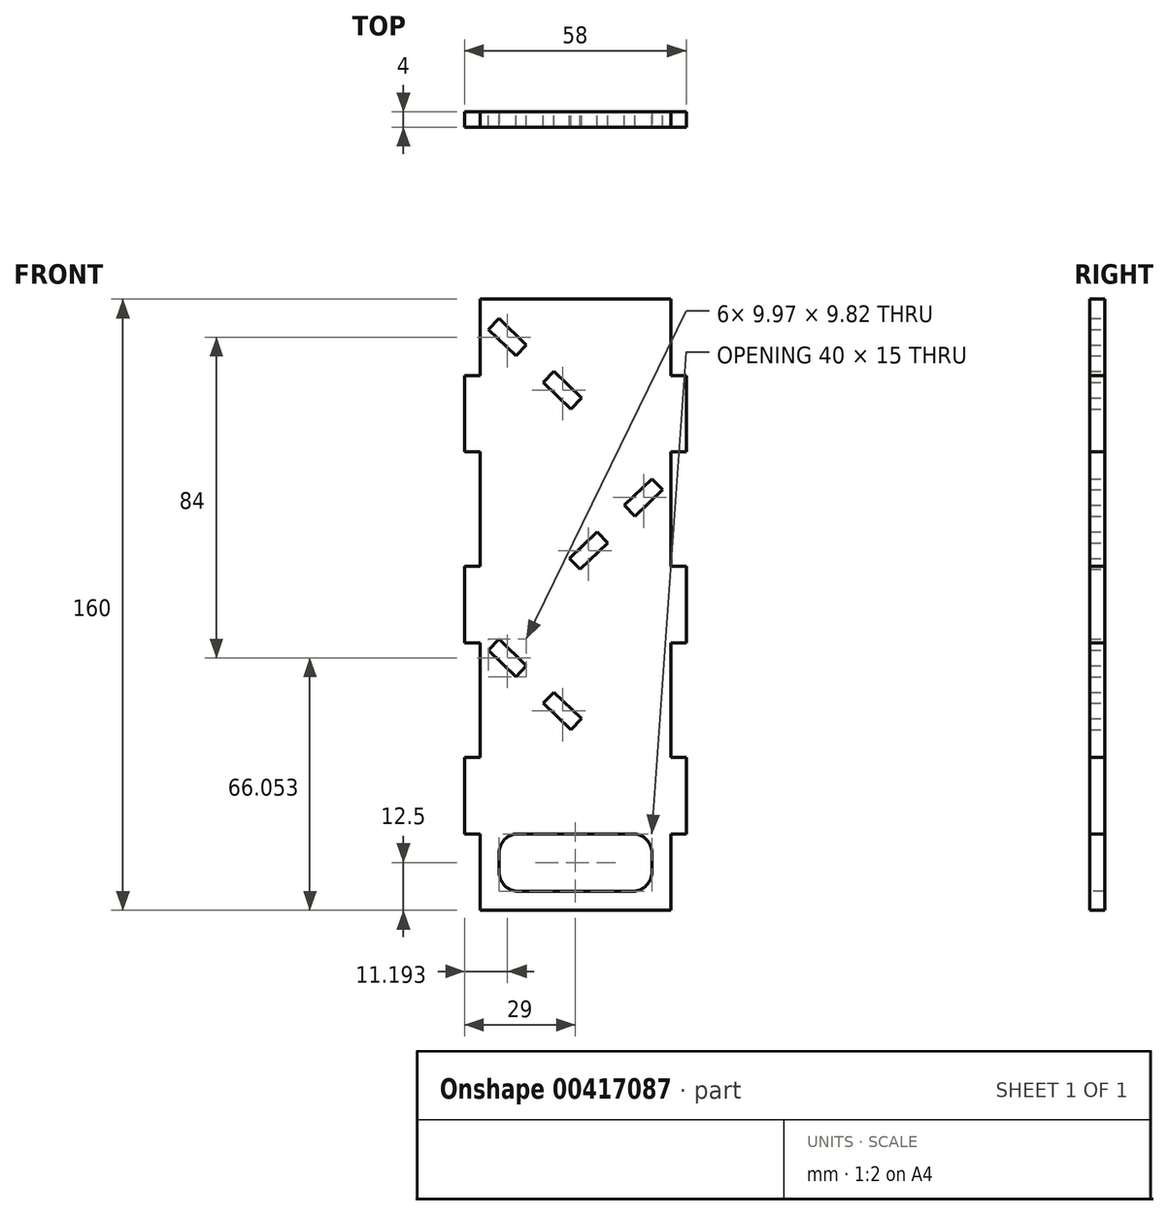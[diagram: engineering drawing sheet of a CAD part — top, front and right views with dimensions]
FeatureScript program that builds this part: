
annotation { "Feature Type Name" : "Feature", "Feature Type Description" : "" }
export const myFeature = defineFeature(function(context is Context, id is Id, definition is map)
    precondition{}
    {
        {
            var Q0;
            Q0=qCreatedBy(makeId("Front.planeOp"),FACE);
            var sketch = newSketch(context, id + "F0", { "sketchPlane" : qUnion([Q0])});
            skLineSegment(sketch, "E0.bottom", {"start": v(25, -80) * mm, "end": v(-25, -80) * mm});
            skLineSegment(sketch, "E0.top", {"start": v(25, 80) * mm, "end": v(-25, 80) * mm});
            skLineSegment(sketch, "E0.left", {"start": v(25, -80) * mm, "end": v(25, 80) * mm});
            skLineSegment(sketch, "E0.right", {"start": v(-25, -80) * mm, "end": v(-25, 80) * mm});
            skPoint(sketch, "E0.middle", {"position": v(0, 0) * mm});
            skLineSegment(sketch, "E1", {"start": v(-25, 77) * mm, "end": v(3.77, 49.21) * mm, "construction": true});
            skLineSegment(sketch, "E2", {"start": v(25, 34.96) * mm, "end": v(-3.77, 7.17) * mm, "construction": true});
            skLineSegment(sketch, "E3", {"start": v(-25, -7.08) * mm, "end": v(3.77, -34.87) * mm, "construction": true});
            skLineSegment(sketch, "E4", {"start": v(-21.4, 73.53) * mm, "end": v(-20.01, 74.97) * mm});
            skLineSegment(sketch, "E5", {"start": v(-20.01, 74.97) * mm, "end": v(-12.82, 68.02) * mm});
            skLineSegment(sketch, "E6", {"start": v(-12.82, 68.02) * mm, "end": v(-14.2, 66.58) * mm});
            skLineSegment(sketch, "E7", {"start": v(-7.02, 59.63) * mm, "end": v(-5.63, 61.07) * mm});
            skLineSegment(sketch, "E8", {"start": v(-5.63, 61.07) * mm, "end": v(1.57, 54.13) * mm});
            skLineSegment(sketch, "E9", {"start": v(1.57, 54.13) * mm, "end": v(0.18, 52.69) * mm});
            skLineSegment(sketch, "E10.MirrorCS", {"start": v(-21.4, 73.53) * mm, "end": v(-22.8, 72.09) * mm});
            skLineSegment(sketch, "E11.MirrorCS", {"start": v(-22.8, 72.09) * mm, "end": v(-15.6, 65.14) * mm});
            skLineSegment(sketch, "E12.MirrorCS", {"start": v(-15.6, 65.14) * mm, "end": v(-14.2, 66.58) * mm});
            skLineSegment(sketch, "E13.MirrorCS", {"start": v(-7.02, 59.63) * mm, "end": v(-8.4, 58.2) * mm});
            skLineSegment(sketch, "E14.MirrorCS", {"start": v(-8.4, 58.2) * mm, "end": v(-1.21, 51.25) * mm});
            skLineSegment(sketch, "E15.MirrorCS", {"start": v(-1.21, 51.25) * mm, "end": v(0.18, 52.69) * mm});
            skLineSegment(sketch, "E16.0.1.0", {"start": v(-8.4, 16.2) * mm, "end": v(-1.21, 9.25) * mm, "construction": true});
            skLineSegment(sketch, "E16.0.1.1", {"start": v(-20.01, 32.97) * mm, "end": v(-12.82, 26.02) * mm, "construction": true});
            skLineSegment(sketch, "E16.0.1.2", {"start": v(-5.63, 19.07) * mm, "end": v(1.57, 12.13) * mm, "construction": true});
            skLineSegment(sketch, "E16.0.1.3", {"start": v(-22.8, 30.09) * mm, "end": v(-15.6, 23.14) * mm, "construction": true});
            skLineSegment(sketch, "E16.0.1.4", {"start": v(-12.82, 26.02) * mm, "end": v(-14.2, 24.58) * mm, "construction": true});
            skLineSegment(sketch, "E16.0.1.5", {"start": v(-7.02, 17.63) * mm, "end": v(-5.63, 19.07) * mm, "construction": true});
            skLineSegment(sketch, "E16.0.1.6", {"start": v(-21.4, 31.53) * mm, "end": v(-20.01, 32.97) * mm, "construction": true});
            skLineSegment(sketch, "E16.0.1.7", {"start": v(-21.4, 31.53) * mm, "end": v(-22.8, 30.09) * mm, "construction": true});
            skLineSegment(sketch, "E16.0.1.8", {"start": v(1.57, 12.13) * mm, "end": v(0.18, 10.69) * mm, "construction": true});
            skLineSegment(sketch, "E16.0.1.9", {"start": v(-15.6, 23.14) * mm, "end": v(-14.2, 24.58) * mm, "construction": true});
            skLineSegment(sketch, "E16.0.1.10", {"start": v(-1.21, 9.25) * mm, "end": v(0.18, 10.69) * mm, "construction": true});
            skLineSegment(sketch, "E16.0.1.11", {"start": v(-7.02, 17.63) * mm, "end": v(-8.4, 16.2) * mm, "construction": true});
            skLineSegment(sketch, "E16.direction1", {"start": v(-22.8, 72.09) * mm, "end": v(2.55, 72.09) * mm, "construction": true});
            skLineSegment(sketch, "E16.direction2", {"start": v(-22.8, 72.09) * mm, "end": v(-22.8, 30.09) * mm, "construction": true});
            skLineSegment(sketch, "E17.0.0.2", {"start": v(-8.4, -25.8) * mm, "end": v(-1.21, -32.75) * mm});
            skLineSegment(sketch, "E17.3.0.2", {"start": v(-20.01, -9.03) * mm, "end": v(-12.82, -15.98) * mm});
            skLineSegment(sketch, "E17.6.0.2", {"start": v(-5.63, -22.93) * mm, "end": v(1.57, -29.87) * mm});
            skLineSegment(sketch, "E17.9.0.2", {"start": v(-22.8, -11.91) * mm, "end": v(-15.6, -18.86) * mm});
            skLineSegment(sketch, "E17.12.0.2", {"start": v(-12.82, -15.98) * mm, "end": v(-14.2, -17.42) * mm});
            skLineSegment(sketch, "E17.15.0.2", {"start": v(-7.02, -24.37) * mm, "end": v(-5.63, -22.93) * mm});
            skLineSegment(sketch, "E17.18.0.2", {"start": v(-21.4, -10.47) * mm, "end": v(-20.01, -9.03) * mm});
            skLineSegment(sketch, "E17.21.0.2", {"start": v(-21.4, -10.47) * mm, "end": v(-22.8, -11.91) * mm});
            skLineSegment(sketch, "E17.24.0.2", {"start": v(1.57, -29.87) * mm, "end": v(0.18, -31.31) * mm});
            skLineSegment(sketch, "E17.27.0.2", {"start": v(-15.6, -18.86) * mm, "end": v(-14.2, -17.42) * mm});
            skLineSegment(sketch, "E17.30.0.2", {"start": v(-1.21, -32.75) * mm, "end": v(0.18, -31.31) * mm});
            skLineSegment(sketch, "E17.33.0.2", {"start": v(-7.02, -24.37) * mm, "end": v(-8.4, -25.8) * mm});
            skLineSegment(sketch, "E18.MirrorCS", {"start": v(21.4, 31.53) * mm, "end": v(22.8, 30.09) * mm});
            skLineSegment(sketch, "E19.MirrorCS", {"start": v(21.4, 31.53) * mm, "end": v(20.01, 32.97) * mm});
            skLineSegment(sketch, "E20.MirrorCS", {"start": v(7.02, 17.63) * mm, "end": v(8.4, 16.2) * mm});
            skLineSegment(sketch, "E21.MirrorCS", {"start": v(15.6, 23.14) * mm, "end": v(14.2, 24.58) * mm});
            skLineSegment(sketch, "E22.MirrorCS", {"start": v(12.82, 26.02) * mm, "end": v(14.2, 24.58) * mm});
            skLineSegment(sketch, "E23.MirrorCS", {"start": v(7.02, 17.63) * mm, "end": v(5.63, 19.07) * mm});
            skLineSegment(sketch, "E24.MirrorCS", {"start": v(-1.57, 12.13) * mm, "end": v(-0.18, 10.69) * mm});
            skLineSegment(sketch, "E25.MirrorCS", {"start": v(1.21, 9.25) * mm, "end": v(-0.18, 10.69) * mm});
            skLineSegment(sketch, "E26.MirrorCS", {"start": v(22.8, 30.09) * mm, "end": v(15.6, 23.14) * mm});
            skLineSegment(sketch, "E27.MirrorCS", {"start": v(8.4, 16.2) * mm, "end": v(1.21, 9.25) * mm});
            skLineSegment(sketch, "E28.MirrorCS", {"start": v(20.01, 32.97) * mm, "end": v(12.82, 26.02) * mm});
            skLineSegment(sketch, "E29.MirrorCS", {"start": v(5.63, 19.07) * mm, "end": v(-1.57, 12.13) * mm});
            skSolve(sketch);
        }
        {
            var Q0;
            Q0=makeQuery(id+"F0.imprint","IMPRINT",FACE,{"disambiguationData":[TD([[makeQuery(id+"F0.imprint","IMPRINT",EDGE,{"derivedFrom":sQuery(id+"F0.wireOp",EDGE,"E0.bottom")}),-1.0]])]});
            extrude(context, id + "F1", {"entities" : qUnion([Q0]), "depth" : 4 * mm});
        }
        {
            var Q0;
            Q0=makeQuery(id+"F1.opExtrude","CAP_FACE",FACE,{"disambiguationData":[OSD([sQuery(id+"F0.wireOp",EDGE,"E0.bottom"),sQuery(id+"F0.wireOp",EDGE,"E0.top"),sQuery(id+"F0.wireOp",EDGE,"E0.left"),sQuery(id+"F0.wireOp",EDGE,"E0.right"),sQuery(id+"F0.wireOp",EDGE,"E4"),sQuery(id+"F0.wireOp",EDGE,"E5"),sQuery(id+"F0.wireOp",EDGE,"E6"),sQuery(id+"F0.wireOp",EDGE,"E7"),sQuery(id+"F0.wireOp",EDGE,"E8"),sQuery(id+"F0.wireOp",EDGE,"E9"),sQuery(id+"F0.wireOp",EDGE,"E10.MirrorCS"),sQuery(id+"F0.wireOp",EDGE,"E11.MirrorCS"),sQuery(id+"F0.wireOp",EDGE,"E12.MirrorCS"),sQuery(id+"F0.wireOp",EDGE,"E13.MirrorCS"),sQuery(id+"F0.wireOp",EDGE,"E14.MirrorCS"),sQuery(id+"F0.wireOp",EDGE,"E15.MirrorCS"),sQuery(id+"F0.wireOp",EDGE,"E17.0.0.2"),sQuery(id+"F0.wireOp",EDGE,"E17.3.0.2"),sQuery(id+"F0.wireOp",EDGE,"E17.6.0.2"),sQuery(id+"F0.wireOp",EDGE,"E17.9.0.2"),sQuery(id+"F0.wireOp",EDGE,"E17.12.0.2"),sQuery(id+"F0.wireOp",EDGE,"E17.15.0.2"),sQuery(id+"F0.wireOp",EDGE,"E17.18.0.2"),sQuery(id+"F0.wireOp",EDGE,"E17.21.0.2"),sQuery(id+"F0.wireOp",EDGE,"E17.24.0.2"),sQuery(id+"F0.wireOp",EDGE,"E17.27.0.2"),sQuery(id+"F0.wireOp",EDGE,"E17.30.0.2"),sQuery(id+"F0.wireOp",EDGE,"E17.33.0.2"),sQuery(id+"F0.wireOp",EDGE,"E18.MirrorCS"),sQuery(id+"F0.wireOp",EDGE,"E19.MirrorCS"),sQuery(id+"F0.wireOp",EDGE,"E20.MirrorCS"),sQuery(id+"F0.wireOp",EDGE,"E21.MirrorCS"),sQuery(id+"F0.wireOp",EDGE,"E22.MirrorCS"),sQuery(id+"F0.wireOp",EDGE,"E23.MirrorCS"),sQuery(id+"F0.wireOp",EDGE,"E24.MirrorCS"),sQuery(id+"F0.wireOp",EDGE,"E25.MirrorCS"),sQuery(id+"F0.wireOp",EDGE,"E26.MirrorCS"),sQuery(id+"F0.wireOp",EDGE,"E27.MirrorCS"),sQuery(id+"F0.wireOp",EDGE,"E28.MirrorCS"),sQuery(id+"F0.wireOp",EDGE,"E29.MirrorCS")])],"isStart":false});
            var sketch = newSketch(context, id + "F2", { "sketchPlane" : qUnion([Q0])});
            skLineSegment(sketch, "E30.bottom", {"start": v(-25, 60) * mm, "end": v(-29, 60) * mm});
            skLineSegment(sketch, "E30.top", {"start": v(-25, 40) * mm, "end": v(-29, 40) * mm});
            skLineSegment(sketch, "E30.left", {"start": v(-25, 60) * mm, "end": v(-25, 40) * mm});
            skLineSegment(sketch, "E30.right", {"start": v(-29, 60) * mm, "end": v(-29, 40) * mm});
            skLineSegment(sketch, "E31.bottom", {"start": v(-25, 0) * mm, "end": v(-29, 0) * mm});
            skLineSegment(sketch, "E31.top", {"start": v(-25, 10) * mm, "end": v(-29, 10) * mm});
            skLineSegment(sketch, "E31.left", {"start": v(-25, 0) * mm, "end": v(-25, 10) * mm});
            skLineSegment(sketch, "E31.right", {"start": v(-29, 0) * mm, "end": v(-29, 10) * mm});
            skLineSegment(sketch, "E32.MirrorCS", {"start": v(-25, -10) * mm, "end": v(-29, -10) * mm});
            skLineSegment(sketch, "E33.MirrorCS", {"start": v(-25, -40) * mm, "end": v(-29, -40) * mm});
            skLineSegment(sketch, "E34.MirrorCS", {"start": v(-25, -60) * mm, "end": v(-29, -60) * mm});
            skLineSegment(sketch, "E35.MirrorCS", {"start": v(-25, 0) * mm, "end": v(-25, -10) * mm});
            skLineSegment(sketch, "E36.MirrorCS", {"start": v(-29, -60) * mm, "end": v(-29, -40) * mm});
            skLineSegment(sketch, "E37.MirrorCS", {"start": v(-25, -60) * mm, "end": v(-25, -40) * mm});
            skLineSegment(sketch, "E38.MirrorCS", {"start": v(-29, 0) * mm, "end": v(-29, -10) * mm});
            skLineSegment(sketch, "E39.MirrorCS", {"start": v(25, 0) * mm, "end": v(29, 0) * mm});
            skLineSegment(sketch, "E40.MirrorCS", {"start": v(25, 10) * mm, "end": v(29, 10) * mm});
            skLineSegment(sketch, "E41.MirrorCS", {"start": v(25, 40) * mm, "end": v(29, 40) * mm});
            skLineSegment(sketch, "E42.MirrorCS", {"start": v(25, 60) * mm, "end": v(29, 60) * mm});
            skLineSegment(sketch, "E43.MirrorCS", {"start": v(25, -10) * mm, "end": v(29, -10) * mm});
            skLineSegment(sketch, "E44.MirrorCS", {"start": v(25, -40) * mm, "end": v(29, -40) * mm});
            skLineSegment(sketch, "E45.MirrorCS", {"start": v(25, -60) * mm, "end": v(29, -60) * mm});
            skLineSegment(sketch, "E46.MirrorCS", {"start": v(25, 0) * mm, "end": v(25, 10) * mm});
            skLineSegment(sketch, "E47.MirrorCS", {"start": v(29, 60) * mm, "end": v(29, 40) * mm});
            skLineSegment(sketch, "E48.MirrorCS", {"start": v(25, 60) * mm, "end": v(25, 40) * mm});
            skLineSegment(sketch, "E49.MirrorCS", {"start": v(29, 0) * mm, "end": v(29, -10) * mm});
            skLineSegment(sketch, "E50.MirrorCS", {"start": v(25, -60) * mm, "end": v(25, -40) * mm});
            skLineSegment(sketch, "E51.MirrorCS", {"start": v(29, -60) * mm, "end": v(29, -40) * mm});
            skLineSegment(sketch, "E52.MirrorCS", {"start": v(29, 0) * mm, "end": v(29, 10) * mm});
            skLineSegment(sketch, "E53.MirrorCS", {"start": v(25, 0) * mm, "end": v(25, -10) * mm});
            skSolve(sketch);
        }
        {
            var Q0;
            Q0 = qSketchRegion(id + "F2", true);
            extrude(context, id + "F3", {"entities" : qUnion([Q0]), "operationType" : NewBodyOperationType.ADD, "oppositeDirection" : true, "depth" : 4 * mm});
        }
        {
            var Q0;
            Q0=makeQuery(id+"F3.boolean.opBoolean","MERGE",FACE,{"derivedFrom":[makeQuery(id+"F1.opExtrude","CAP_FACE",FACE,{"disambiguationData":[OSD([sQuery(id+"F0.wireOp",EDGE,"E0.bottom"),sQuery(id+"F0.wireOp",EDGE,"E0.top"),sQuery(id+"F0.wireOp",EDGE,"E0.left"),sQuery(id+"F0.wireOp",EDGE,"E0.right"),sQuery(id+"F0.wireOp",EDGE,"E4"),sQuery(id+"F0.wireOp",EDGE,"E5"),sQuery(id+"F0.wireOp",EDGE,"E6"),sQuery(id+"F0.wireOp",EDGE,"E7"),sQuery(id+"F0.wireOp",EDGE,"E8"),sQuery(id+"F0.wireOp",EDGE,"E9"),sQuery(id+"F0.wireOp",EDGE,"E10.MirrorCS"),sQuery(id+"F0.wireOp",EDGE,"E11.MirrorCS"),sQuery(id+"F0.wireOp",EDGE,"E12.MirrorCS"),sQuery(id+"F0.wireOp",EDGE,"E13.MirrorCS"),sQuery(id+"F0.wireOp",EDGE,"E14.MirrorCS"),sQuery(id+"F0.wireOp",EDGE,"E15.MirrorCS"),sQuery(id+"F0.wireOp",EDGE,"E17.0.0.2"),sQuery(id+"F0.wireOp",EDGE,"E17.3.0.2"),sQuery(id+"F0.wireOp",EDGE,"E17.6.0.2"),sQuery(id+"F0.wireOp",EDGE,"E17.9.0.2"),sQuery(id+"F0.wireOp",EDGE,"E17.12.0.2"),sQuery(id+"F0.wireOp",EDGE,"E17.15.0.2"),sQuery(id+"F0.wireOp",EDGE,"E17.18.0.2"),sQuery(id+"F0.wireOp",EDGE,"E17.21.0.2"),sQuery(id+"F0.wireOp",EDGE,"E17.24.0.2"),sQuery(id+"F0.wireOp",EDGE,"E17.27.0.2"),sQuery(id+"F0.wireOp",EDGE,"E17.30.0.2"),sQuery(id+"F0.wireOp",EDGE,"E17.33.0.2"),sQuery(id+"F0.wireOp",EDGE,"E18.MirrorCS"),sQuery(id+"F0.wireOp",EDGE,"E19.MirrorCS"),sQuery(id+"F0.wireOp",EDGE,"E20.MirrorCS"),sQuery(id+"F0.wireOp",EDGE,"E21.MirrorCS"),sQuery(id+"F0.wireOp",EDGE,"E22.MirrorCS"),sQuery(id+"F0.wireOp",EDGE,"E23.MirrorCS"),sQuery(id+"F0.wireOp",EDGE,"E24.MirrorCS"),sQuery(id+"F0.wireOp",EDGE,"E25.MirrorCS"),sQuery(id+"F0.wireOp",EDGE,"E26.MirrorCS"),sQuery(id+"F0.wireOp",EDGE,"E27.MirrorCS"),sQuery(id+"F0.wireOp",EDGE,"E28.MirrorCS"),sQuery(id+"F0.wireOp",EDGE,"E29.MirrorCS")])],"isStart":false}),makeQuery(id+"F3.opExtrude","CAP_FACE",FACE,{"disambiguationData":[OSD([sQuery(id+"F2.wireOp",EDGE,"E30.bottom"),sQuery(id+"F2.wireOp",EDGE,"E30.top"),sQuery(id+"F2.wireOp",EDGE,"E30.left"),sQuery(id+"F2.wireOp",EDGE,"E30.right")])],"isStart":true}),makeQuery(id+"F3.opExtrude","CAP_FACE",FACE,{"disambiguationData":[OSD([sQuery(id+"F2.wireOp",EDGE,"E31.top"),sQuery(id+"F2.wireOp",EDGE,"E31.left"),sQuery(id+"F2.wireOp",EDGE,"E31.right"),sQuery(id+"F2.wireOp",EDGE,"E32.MirrorCS"),sQuery(id+"F2.wireOp",EDGE,"E35.MirrorCS"),sQuery(id+"F2.wireOp",EDGE,"E38.MirrorCS")])],"isStart":true}),makeQuery(id+"F3.opExtrude","CAP_FACE",FACE,{"disambiguationData":[OSD([sQuery(id+"F2.wireOp",EDGE,"E33.MirrorCS"),sQuery(id+"F2.wireOp",EDGE,"E34.MirrorCS"),sQuery(id+"F2.wireOp",EDGE,"E36.MirrorCS"),sQuery(id+"F2.wireOp",EDGE,"E37.MirrorCS")])],"isStart":true}),makeQuery(id+"F3.opExtrude","CAP_FACE",FACE,{"disambiguationData":[OSD([sQuery(id+"F2.wireOp",EDGE,"E40.MirrorCS"),sQuery(id+"F2.wireOp",EDGE,"E43.MirrorCS"),sQuery(id+"F2.wireOp",EDGE,"E46.MirrorCS"),sQuery(id+"F2.wireOp",EDGE,"E49.MirrorCS"),sQuery(id+"F2.wireOp",EDGE,"E52.MirrorCS"),sQuery(id+"F2.wireOp",EDGE,"E53.MirrorCS")])],"isStart":true}),makeQuery(id+"F3.opExtrude","CAP_FACE",FACE,{"disambiguationData":[OSD([sQuery(id+"F2.wireOp",EDGE,"E41.MirrorCS"),sQuery(id+"F2.wireOp",EDGE,"E42.MirrorCS"),sQuery(id+"F2.wireOp",EDGE,"E47.MirrorCS"),sQuery(id+"F2.wireOp",EDGE,"E48.MirrorCS")])],"isStart":true}),makeQuery(id+"F3.opExtrude","CAP_FACE",FACE,{"disambiguationData":[OSD([sQuery(id+"F2.wireOp",EDGE,"E44.MirrorCS"),sQuery(id+"F2.wireOp",EDGE,"E45.MirrorCS"),sQuery(id+"F2.wireOp",EDGE,"E50.MirrorCS"),sQuery(id+"F2.wireOp",EDGE,"E51.MirrorCS")])],"isStart":true})]});
            var sketch = newSketch(context, id + "F4", { "sketchPlane" : qUnion([Q0])});
            skLineSegment(sketch, "E54.bottom", {"start": v(20, -75) * mm, "end": v(-20, -75) * mm});
            skLineSegment(sketch, "E54.top", {"start": v(20, -60) * mm, "end": v(-20, -60) * mm});
            skLineSegment(sketch, "E54.left", {"start": v(20, -75) * mm, "end": v(20, -60) * mm});
            skLineSegment(sketch, "E54.right", {"start": v(-20, -75) * mm, "end": v(-20, -60) * mm});
            skPoint(sketch, "E54.middle", {"position": v(0, -67.5) * mm});
            skSolve(sketch);
        }
        {
            var Q0;
            Q0=makeQuery(id+"F4.imprint","IMPRINT",FACE,{"disambiguationData":[TD([[makeQuery(id+"F4.imprint","IMPRINT",EDGE,{"derivedFrom":sQuery(id+"F4.wireOp",EDGE,"E54.bottom")}),-1.0]])]});
            extrude(context, id + "F5", {"entities" : qUnion([Q0]), "operationType" : NewBodyOperationType.REMOVE, "oppositeDirection" : true, "depth" : 25 * mm});
        }
        {
            var Q0;
            Q0=makeQuery(id+"F5.boolean.opBoolean","COPY",EDGE,{"derivedFrom":makeQuery(id+"F5.opExtrude","SWEPT_EDGE",EDGE,{"disambiguationData":[OSD([sQuery(id+"F4.wireOp",EDGE,"E54.top"),sQuery(id+"F4.wireOp",EDGE,"E54.right")])]})});
            var Q1;
            Q1=makeQuery(id+"F5.boolean.opBoolean","COPY",EDGE,{"derivedFrom":makeQuery(id+"F5.opExtrude","SWEPT_EDGE",EDGE,{"disambiguationData":[OSD([sQuery(id+"F4.wireOp",EDGE,"E54.top"),sQuery(id+"F4.wireOp",EDGE,"E54.left")])]})});
            var Q2;
            Q2=makeQuery(id+"F5.boolean.opBoolean","COPY",EDGE,{"derivedFrom":makeQuery(id+"F5.opExtrude","SWEPT_EDGE",EDGE,{"disambiguationData":[OSD([sQuery(id+"F4.wireOp",EDGE,"E54.bottom"),sQuery(id+"F4.wireOp",EDGE,"E54.left")])]})});
            var Q3;
            Q3=makeQuery(id+"F5.boolean.opBoolean","COPY",EDGE,{"derivedFrom":makeQuery(id+"F5.opExtrude","SWEPT_EDGE",EDGE,{"disambiguationData":[OSD([sQuery(id+"F4.wireOp",EDGE,"E54.bottom"),sQuery(id+"F4.wireOp",EDGE,"E54.right")])]})});
            fillet(context, id + "F6", {"entities" : qUnion([Q0, Q1, Q2, Q3]), "radius" : 5 * mm, "tangentPropagation" : true, "allowEdgeOverflow" : false});
        }
    });
